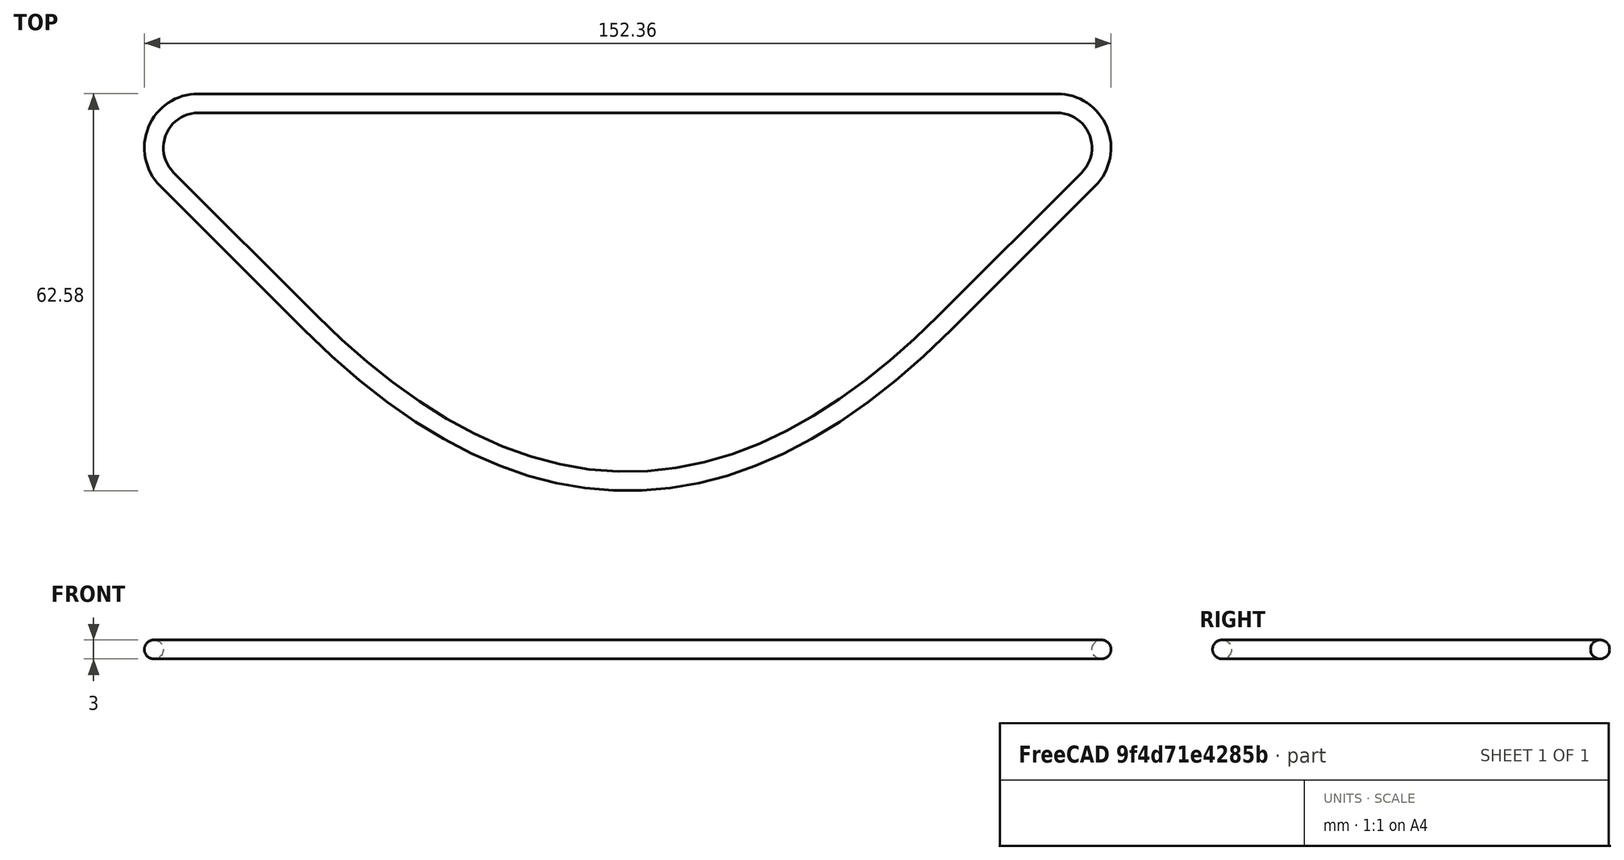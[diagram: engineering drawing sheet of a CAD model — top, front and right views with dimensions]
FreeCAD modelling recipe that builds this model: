
FCSTD DOCUMENT  (FreeCAD 1.1R20260108 (Git shallow))
Label: Sketcher_ArcOfParabola
License: Public Domain
LicenseURL: https://en.wikipedia.org/wiki/Public_domain
objects: Sketcher::SketchObject×2, App::Point×1, PartDesign::AdditivePipe×1, PartDesign::Body×1
note: 8 computed .brp shape members not serialized (recipe doc carries the construction recipe); baked Part::Feature solids carry a one-line shape summary decoded from their .brp

FEATURE [App::Point] Origin001
  Role = Origin
FEATURE [Sketcher::SketchObject] Sketch
  ArcFitTolerance = 1e-06
  AttachmentSupport = -> [Origin]
  ExternalTypes = [0]
  FullyConstrained = true
  MakeInternals = false
  MapMode = 5
  sketch-geometry (8):
    g0: ArcOfParabola CenterX=0 CenterY=-25 CenterZ=0 NormalX=0 NormalY=0 NormalZ=1 Focal=25 AngleXU=1.5708 StartAngle=-50 EndAngle=50
    g1: GeomPoint [constr] X=0 Y=0 Z=0
    g2: LineSegment [constr] StartX=0 StartY=-25 StartZ=0 EndX=0 EndY=0 EndZ=0
    g3: LineSegment StartX=-50 StartY=5.578e-13 StartZ=0 EndX=-72.6274 EndY=22.6274 EndZ=0
    g4: LineSegment StartX=50 StartY=9.95e-14 StartZ=0 EndX=72.6274 EndY=22.6274 EndZ=0
    g5: ArcOfCircle CenterX=-67.6777 CenterY=27.5772 CenterZ=0 NormalX=0 NormalY=0 NormalZ=1 AngleXU=0 Radius=7 StartAngle=1.5708 EndAngle=3.92699
    g6: ArcOfCircle CenterX=67.6777 CenterY=27.5772 CenterZ=0 NormalX=0 NormalY=0 NormalZ=1 AngleXU=0 Radius=7 StartAngle=5.49779 EndAngle=7.85398
    g7: LineSegment StartX=-67.6777 StartY=34.5772 StartZ=0 EndX=67.6777 EndY=34.5772 EndZ=0
  constraints (17):
    c: InternalAlignment(g1,g0)
    c: InternalAlignment(g2,g0)
    c: Coincident(g1,g-1)
    c: PointOnObject(g0,g-2)
    c: PointOnObject(g0,g-1)
    c: PointOnObject(g0,g-1)
    c: DistanceY(g2,g2) = 25
    c: Tangent(g3,g0) = -1.5708
    c: Tangent(g4,g0) = 1.5708
    c: Tangent(g5,g3) = 1.5708
    c: Tangent(g6,g4) = -1.5708
    c: Radius(g5) = 7
    c: Equal(g5,g6)
    c: Horizontal(g7)
    c: Tangent(g7,g5) = 1.5708
    c: Tangent(g7,g6) = 1.5708
    c: Distance(g3,g3) = 32
FEATURE [Sketcher::SketchObject] Sketch001
  ArcFitTolerance = 1e-06
  AttachmentSupport = -> [Origin]
  ExternalGeometry = -> [Sketch]
  ExternalTypes = [0]
  FullyConstrained = true
  MakeInternals = false
  MapMode = 5
  Placement = pos=(0,0,0) rot=(0.57735,0.57735,0.57735;2.0944rad)
  sketch-geometry (1):
    g0: Circle CenterX=34.5772 CenterY=0 CenterZ=0 NormalX=0 NormalY=0 NormalZ=1 AngleXU=0 Radius=1.5
  constraints (2):
    c: Coincident(g0,g-3)
    c: Diameter(g0) = 3
FEATURE [PartDesign::AdditivePipe] AdditivePipe
  AuxiliaryCurvilinear = true
  AuxiliarySpineTangent = false
  Binormal = (0,0,0)
  Mode = 0
  Profile = -> Sketch001
  Refine = true
  Spine = -> Sketch
  SpineTangent = false
  Suppressed = false
  Transformation = 0
  Transition = 0
FEATURE [PartDesign::Body] Body
  AllowCompound = true
  Group = -> [Sketch,Sketch001,AdditivePipe]
  Origin = -> Origin
  Tip = -> AdditivePipe
